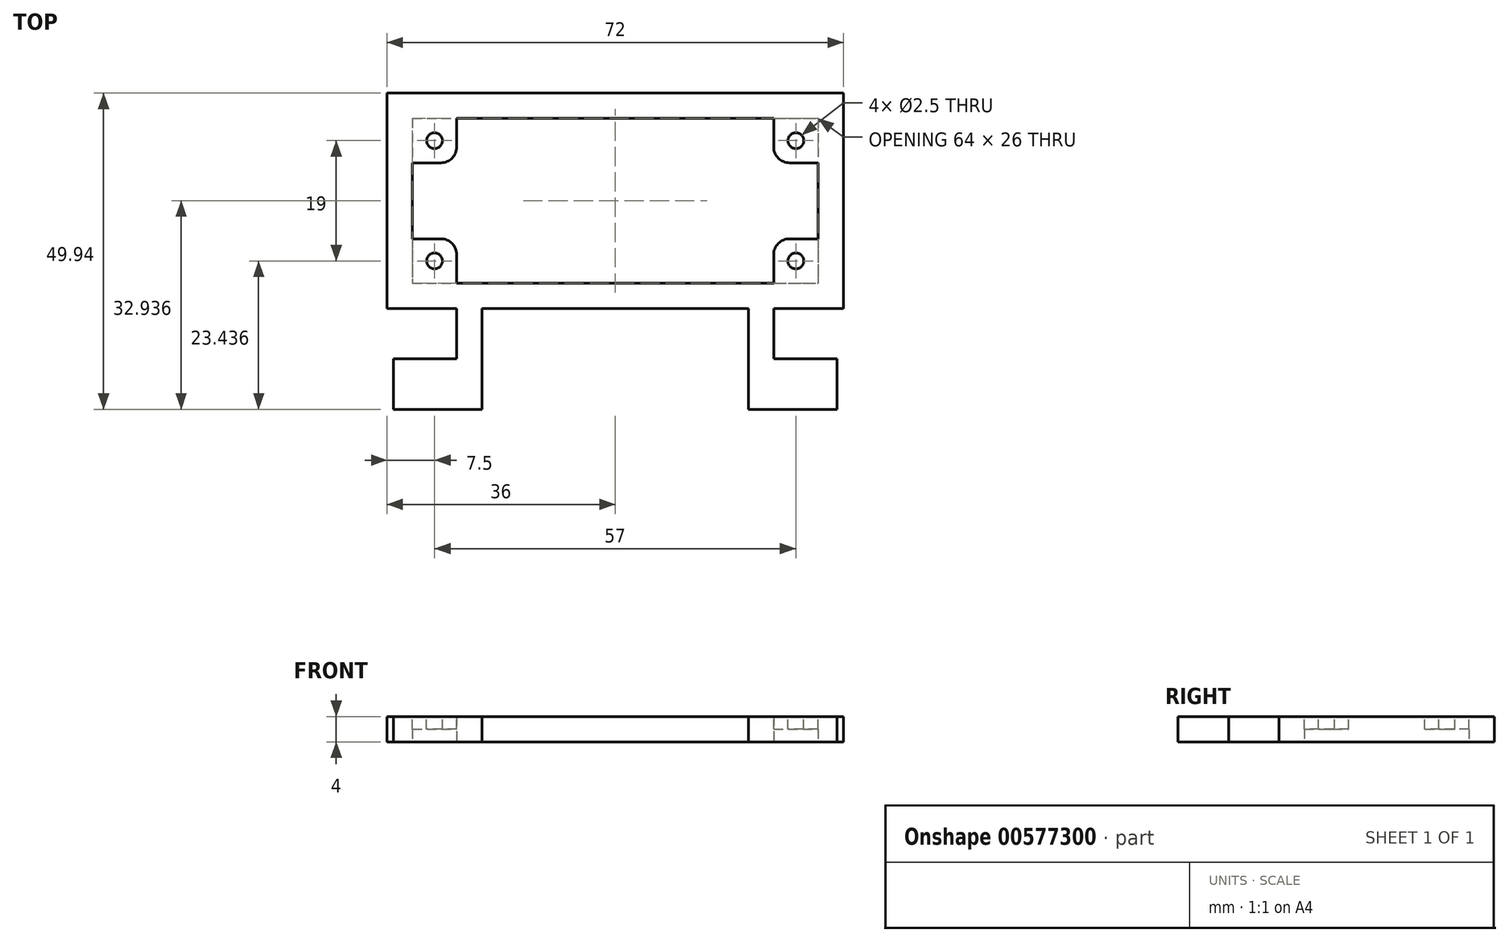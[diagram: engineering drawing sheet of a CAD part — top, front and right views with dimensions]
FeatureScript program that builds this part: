
annotation { "Feature Type Name" : "Feature", "Feature Type Description" : "" }
export const myFeature = defineFeature(function(context is Context, id is Id, definition is map)
    precondition{}
    {
        {
            var Q0;
            Q0=qCreatedBy(makeId("Top.planeOp"),FACE);
            var sketch = newSketch(context, id + "F0", { "sketchPlane" : qUnion([Q0])});
            skLineSegment(sketch, "E0.bottom", {"start": v(25, -30) * mm, "end": v(35, -30) * mm});
            skLineSegment(sketch, "E0.top", {"start": v(25, -22) * mm, "end": v(35, -22) * mm});
            skLineSegment(sketch, "E0.right", {"start": v(35, -30) * mm, "end": v(35, -22) * mm});
            skLineSegment(sketch, "E1.bottom", {"start": v(0, 15.94) * mm, "end": v(32, 15.94) * mm});
            skLineSegment(sketch, "E1.top", {"start": v(0, -10.06) * mm, "end": v(32, -10.06) * mm});
            skLineSegment(sketch, "E1.right", {"start": v(32, 15.94) * mm, "end": v(32, -10.06) * mm});
            skLineSegment(sketch, "E2", {"start": v(25, -30) * mm, "end": v(21, -30) * mm});
            skLineSegment(sketch, "E3", {"start": v(21, -30) * mm, "end": v(21, -14.06) * mm});
            skLineSegment(sketch, "E4", {"start": v(21, -14.06) * mm, "end": v(0, -14.06) * mm});
            skLineSegment(sketch, "E5", {"start": v(0, -14.06) * mm, "end": v(0, -10.06) * mm});
            skLineSegment(sketch, "E6", {"start": v(25, -22) * mm, "end": v(25, -14.06) * mm});
            skLineSegment(sketch, "E7", {"start": v(25, -14.06) * mm, "end": v(36, -14.06) * mm});
            skLineSegment(sketch, "E8", {"start": v(36, -14.06) * mm, "end": v(36, 19.94) * mm});
            skLineSegment(sketch, "E9", {"start": v(36, 19.94) * mm, "end": v(0, 19.94) * mm});
            skLineSegment(sketch, "E10", {"start": v(0, 19.94) * mm, "end": v(0, 15.94) * mm});
            skSolve(sketch);
        }
        {
            var Q0;
            Q0 = qSketchRegion(id + "F0", true);
            extrude(context, id + "F1", {"entities" : qUnion([Q0]), "depth" : 4 * mm, "offsetDistance" : 25 * mm});
        }
        {
            var Q0;
            Q0=makeQuery(id+"F1.opExtrude","SWEPT_BODY",BODY,{"disambiguationData":[OSD([sQuery(id+"F0.wireOp",EDGE,"aGSBdWBT-oQxI-juCk-IGnG-ylojRgTnqDs5.bottom"),sQuery(id+"F0.wireOp",EDGE,"aGSBdWBT-oQxI-juCk-IGnG-ylojRgTnqDs5.top"),sQuery(id+"F0.wireOp",EDGE,"aGSBdWBT-oQxI-juCk-IGnG-ylojRgTnqDs5.left"),sQuery(id+"F0.wireOp",EDGE,"aGSBdWBT-oQxI-juCk-IGnG-ylojRgTnqDs5.right"),sQuery(id+"F0.wireOp",EDGE,"E0.bottom"),sQuery(id+"F0.wireOp",EDGE,"E0.top"),sQuery(id+"F0.wireOp",EDGE,"E0.right"),sQuery(id+"F0.wireOp",EDGE,"btqqvYaL-MnXf-Kxdd-G4pG-ooeZZcjjSskU.bottom"),sQuery(id+"F0.wireOp",EDGE,"btqqvYaL-MnXf-Kxdd-G4pG-ooeZZcjjSskU.top"),sQuery(id+"F0.wireOp",EDGE,"btqqvYaL-MnXf-Kxdd-G4pG-ooeZZcjjSskU.right"),sQuery(id+"F0.wireOp",EDGE,"aa26d452-cda6-4e70-ae36-6e496a84bcd4.trimOffspring")])]});
            var Q1;
            Q1=qCreatedBy(makeId("Right.planeOp"),FACE);
            mirror(context, id + "F2", {"operationType" : NewBodyOperationType.ADD, "entities" : qUnion([Q0]), "mirrorPlane" : qUnion([Q1])});
        }
        {
            var Q0;
            {var subQ0=makeQuery(id+"F1.opExtrude","CAP_FACE",FACE,{"disambiguationData":[OSD([sQuery(id+"F0.wireOp",EDGE,"E0.bottom"),sQuery(id+"F0.wireOp",EDGE,"E0.top"),sQuery(id+"F0.wireOp",EDGE,"E0.right"),sQuery(id+"F0.wireOp",EDGE,"E1.bottom"),sQuery(id+"F0.wireOp",EDGE,"E1.top"),sQuery(id+"F0.wireOp",EDGE,"E1.right"),sQuery(id+"F0.wireOp",EDGE,"E2"),sQuery(id+"F0.wireOp",EDGE,"E3"),sQuery(id+"F0.wireOp",EDGE,"E4"),sQuery(id+"F0.wireOp",EDGE,"E5"),sQuery(id+"F0.wireOp",EDGE,"E6"),sQuery(id+"F0.wireOp",EDGE,"E7"),sQuery(id+"F0.wireOp",EDGE,"E8"),sQuery(id+"F0.wireOp",EDGE,"E9"),sQuery(id+"F0.wireOp",EDGE,"E10")])],"isStart":false});Q0=makeQuery(id+"F2.boolean.opBoolean","MERGE",FACE,{"derivedFrom":[subQ0,makeQuery(id+"F2.opPattern","COPY",FACE,{"derivedFrom":subQ0,"instanceName":"1"})]});}
            var sketch = newSketch(context, id + "F3", { "sketchPlane" : qUnion([Q0])});
            skLineSegment(sketch, "E11.bottom", {"start": v(-32, -10.06) * mm, "end": v(-25, -10.06) * mm});
            skLineSegment(sketch, "E11.top", {"start": v(-32, -3.06) * mm, "end": v(-27.5, -3.06) * mm});
            skLineSegment(sketch, "E11.left", {"start": v(-32, -10.06) * mm, "end": v(-32, -3.06) * mm});
            skLineSegment(sketch, "E11.right", {"start": v(-25, -10.06) * mm, "end": v(-25, -5.56) * mm});
            skLineSegment(sketch, "E12.bottom", {"start": v(-32, 15.94) * mm, "end": v(-25, 15.94) * mm});
            skLineSegment(sketch, "E12.top", {"start": v(-32, 8.94) * mm, "end": v(-27.5, 8.94) * mm});
            skLineSegment(sketch, "E12.left", {"start": v(-32, 15.94) * mm, "end": v(-32, 8.94) * mm});
            skLineSegment(sketch, "E12.right", {"start": v(-25, 15.94) * mm, "end": v(-25, 11.44) * mm});
            skLineSegment(sketch, "E13.bottom", {"start": v(32, 15.94) * mm, "end": v(25, 15.94) * mm});
            skLineSegment(sketch, "E13.top", {"start": v(32, 8.94) * mm, "end": v(27.5, 8.94) * mm});
            skLineSegment(sketch, "E13.left", {"start": v(32, 15.94) * mm, "end": v(32, 8.94) * mm});
            skLineSegment(sketch, "E13.right", {"start": v(25, 15.94) * mm, "end": v(25, 11.44) * mm});
            skPoint(sketch, "E14.oppositeSnap0", {"position": v(25, 12.44) * mm});
            skLineSegment(sketch, "E14.bottom", {"start": v(32, -10.06) * mm, "end": v(25, -10.06) * mm});
            skLineSegment(sketch, "E14.top", {"start": v(32, -3.06) * mm, "end": v(27.5, -3.06) * mm});
            skLineSegment(sketch, "E14.left", {"start": v(32, -10.06) * mm, "end": v(32, -3.06) * mm});
            skLineSegment(sketch, "E14.right", {"start": v(25, -10.06) * mm, "end": v(25, -5.56) * mm});
            skCircle(sketch, "E15", {"center": v(-28.5, -6.56) * mm, "radius": 1.25 * mm});
            skPoint(sketch, "E15.centerSnap0", {"position": v(-25, -6.56) * mm});
            skPoint(sketch, "E15.centerSnap1", {"position": v(-28.5, -3.06) * mm});
            skCircle(sketch, "E16", {"center": v(-28.5, 12.44) * mm, "radius": 1.25 * mm});
            skPoint(sketch, "E16.centerSnap0", {"position": v(-25, 12.44) * mm});
            skCircle(sketch, "E17", {"center": v(28.5, 12.44) * mm, "radius": 1.25 * mm});
            skPoint(sketch, "E17.centerSnap0", {"position": v(28.5, 8.94) * mm});
            skCircle(sketch, "E18", {"center": v(28.5, -6.56) * mm, "radius": 1.25 * mm});
            skPoint(sketch, "E18.centerSnap0", {"position": v(28.5, -3.06) * mm});
            skPoint(sketch, "E19.visualSharp", {"position": v(-25, -3.06) * mm});
            skArc(sketch, "E19.filletArc", {"start": v(-25, -5.56) * mm, "mid": v(-25.73, -3.8) * mm, "end": v(-27.5, -3.06) * mm});
            skPoint(sketch, "E20.visualSharp", {"position": v(-25, 8.94) * mm});
            skArc(sketch, "E20.filletArc", {"start": v(-27.5, 8.94) * mm, "mid": v(-25.73, 9.67) * mm, "end": v(-25, 11.44) * mm});
            skPoint(sketch, "E21.visualSharp", {"position": v(25, 8.94) * mm});
            skArc(sketch, "E21.filletArc", {"start": v(25, 11.44) * mm, "mid": v(25.73, 9.67) * mm, "end": v(27.5, 8.94) * mm});
            skPoint(sketch, "E22.visualSharp", {"position": v(25, -3.06) * mm});
            skArc(sketch, "E22.filletArc", {"start": v(27.5, -3.06) * mm, "mid": v(25.73, -3.8) * mm, "end": v(25, -5.56) * mm});
            skSolve(sketch);
        }
        {
            var Q0;
            Q0 = qSketchRegion(id + "F3", true);
            extrude(context, id + "F4", {"entities" : qUnion([Q0]), "operationType" : NewBodyOperationType.ADD, "oppositeDirection" : true, "depth" : 2 * mm, "offsetDistance" : 25 * mm});
        }
    });
